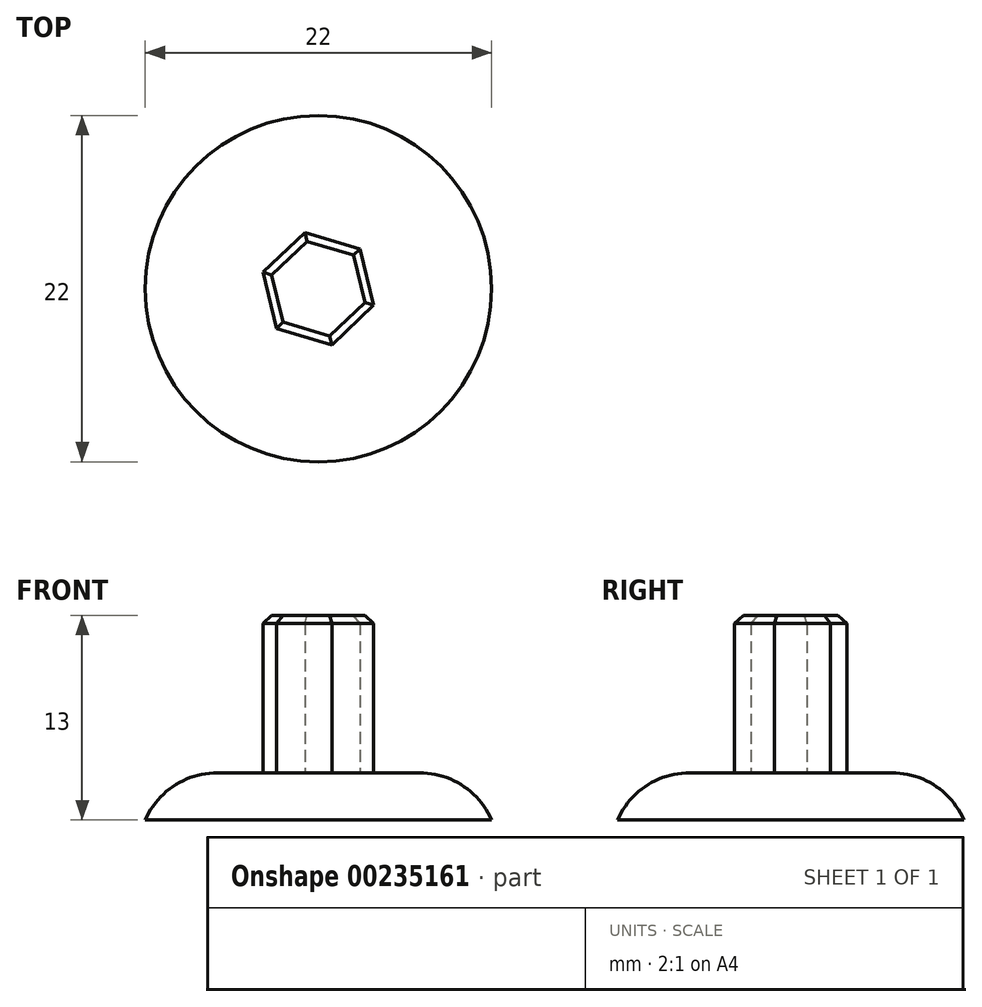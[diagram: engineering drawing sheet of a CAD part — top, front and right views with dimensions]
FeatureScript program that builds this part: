
annotation { "Feature Type Name" : "Feature", "Feature Type Description" : "" }
export const myFeature = defineFeature(function(context is Context, id is Id, definition is map)
    precondition{}
    {
        {
            var Q0;
            Q0=qCreatedBy(makeId("Top.planeOp"),FACE);
            var sketch = newSketch(context, id + "F0", { "sketchPlane" : qUnion([Q0])});
            skCircle(sketch, "E0", {"center": v(0, 0) * mm, "radius": 11 * mm});
            skSolve(sketch);
        }
        {
            var Q0;
            Q0 = qSketchRegion(id + "F0", true);
            extrude(context, id + "F1", {"entities" : qUnion([Q0]), "depth" : 3 * mm});
        }
        {
            var Q0;
            Q0=makeQuery(id+"F1.opExtrude","CAP_FACE",FACE,{"disambiguationData":[OSD([sQuery(id+"F0.wireOp",EDGE,"E0")])],"isStart":false});
            var sketch = newSketch(context, id + "F2", { "sketchPlane" : qUnion([Q0])});
            skCircle(sketch, "E1.cCircle", {"center": v(0, 0) * mm, "radius": 3.17 * mm, "construction": true});
            skLineSegment(sketch, "E1.0", {"start": v(3.52, -1.04) * mm, "end": v(0.86, -3.56) * mm});
            skLineSegment(sketch, "E1.1", {"start": v(0.86, -3.56) * mm, "end": v(-2.66, -2.52) * mm});
            skLineSegment(sketch, "E1.2", {"start": v(-2.66, -2.52) * mm, "end": v(-3.52, 1.04) * mm});
            skLineSegment(sketch, "E1.3", {"start": v(-3.52, 1.04) * mm, "end": v(-0.86, 3.56) * mm});
            skLineSegment(sketch, "E1.4", {"start": v(-0.86, 3.56) * mm, "end": v(2.66, 2.52) * mm});
            skLineSegment(sketch, "E1.5", {"start": v(2.66, 2.52) * mm, "end": v(3.52, -1.04) * mm});
            skPoint(sketch, "E1.0.midPoint", {"position": v(2.19, -2.3) * mm});
            skSolve(sketch);
        }
        {
            var Q0;
            Q0=makeQuery(id+"F2.imprint","IMPRINT",FACE,{"disambiguationData":[TD([[makeQuery(id+"F2.imprint","IMPRINT",EDGE,{"derivedFrom":sQuery(id+"F2.wireOp",EDGE,"E1.0")}),-1.0]])]});
            extrude(context, id + "F3", {"entities" : qUnion([Q0]), "operationType" : NewBodyOperationType.ADD, "depth" : 10 * mm});
        }
        {
            var Q0;
            Q0=makeQuery(id+"F3.opExtrude","CAP_EDGE",EDGE,{"disambiguationData":[OSD([sQuery(id+"F2.wireOp",EDGE,"E1.0")])],"isStart":false});
            var Q1;
            Q1=makeQuery(id+"F3.opExtrude","CAP_EDGE",EDGE,{"disambiguationData":[OSD([sQuery(id+"F2.wireOp",EDGE,"E1.5")])],"isStart":false});
            var Q2;
            Q2=makeQuery(id+"F3.opExtrude","CAP_EDGE",EDGE,{"disambiguationData":[OSD([sQuery(id+"F2.wireOp",EDGE,"E1.4")])],"isStart":false});
            var Q3;
            Q3=makeQuery(id+"F3.opExtrude","CAP_EDGE",EDGE,{"disambiguationData":[OSD([sQuery(id+"F2.wireOp",EDGE,"E1.3")])],"isStart":false});
            var Q4;
            Q4=makeQuery(id+"F3.opExtrude","CAP_EDGE",EDGE,{"disambiguationData":[OSD([sQuery(id+"F2.wireOp",EDGE,"E1.2")])],"isStart":false});
            var Q5;
            Q5=makeQuery(id+"F3.opExtrude","CAP_EDGE",EDGE,{"disambiguationData":[OSD([sQuery(id+"F2.wireOp",EDGE,"E1.1")])],"isStart":false});
            chamfer(context, id + "F4", {"entities" : qUnion([Q0, Q1, Q2, Q3, Q4, Q5]), "width" : 0.5 * mm, "tangentPropagation" : true});
        }
        {
            var Q0;
            Q0=makeQuery(id+"F1.opExtrude","CAP_EDGE",EDGE,{"disambiguationData":[OSD([sQuery(id+"F0.wireOp",EDGE,"E0")])],"isStart":false});
            fillet(context, id + "F5", {"entities" : qUnion([Q0]), "radius" : 5 * mm, "tangentPropagation" : true, "allowEdgeOverflow" : false});
        }
    });
